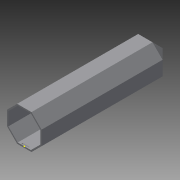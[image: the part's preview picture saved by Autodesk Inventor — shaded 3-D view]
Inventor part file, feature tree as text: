
AUTODESK INVENTOR PART (.ipt)
format: ipt  version: 2015 SP2 (Build 190223200, 223)  size: 187,392 bytes
history: native  units: mm
features: sketch x5, extrude x3, chamfer x2, plane x1, loft x1, shell x1, other x1
ambient origin geometry x8: Origin, YZ Plane, XZ Plane, XY Plane, X Axis, Y Axis, Z Axis, Center Point
bodies: Solid1 (feature_tree)
feature tree (14):
  extrude  "Extrusion1"  Depth=175.0mm TaperAngle=0.0deg
  plane  "Work Plane1"
  loft  "Loft1"
  shell  "Shell2"  Thickness=20.0mm
  sketch  "Sketch7"  dims[d7=0.0mm d8=90.0deg d9=0.0mm d10=90.0deg]
  sketch  "Sketch8"  dims[d13=2.0mm d14=10.0mm]
  extrude  "Extrusion2"  TaperAngle=0.0deg  [1 undecoded]
  extrude  "Extrusion3"  Depth=10.0mm
  chamfer  "Chamfer1"  Distance=2.0mm
  chamfer  "Chamfer2"  Distance=10.0mm
  sketch  "Sketch1"  dims[d0=50.0mm d1=175.0mm d2=0.0mm]
  sketch  "Sketch2"  dims[d4=15.0mm d5=20.0mm d6=20.0mm]
  other  "Edges1"
  sketch  "Sketch9"  dims[d15=2.5mm d16=2.0mm d17=10.0mm d18=2.5mm d19=2.0mm d20=1.0mm d21=0.0mm d22=1.0mm d23=0.0mm d24=1.0mm d25=2.0mm d26=6.108652mm d27=1.0mm d28=2.0mm d29=6.108652mm]
note: 1 required parameter value undecoded (feature->parameter linkage not recoverable at this tier; creation-order binding heuristic only, values carry confidence <= 0.55)
